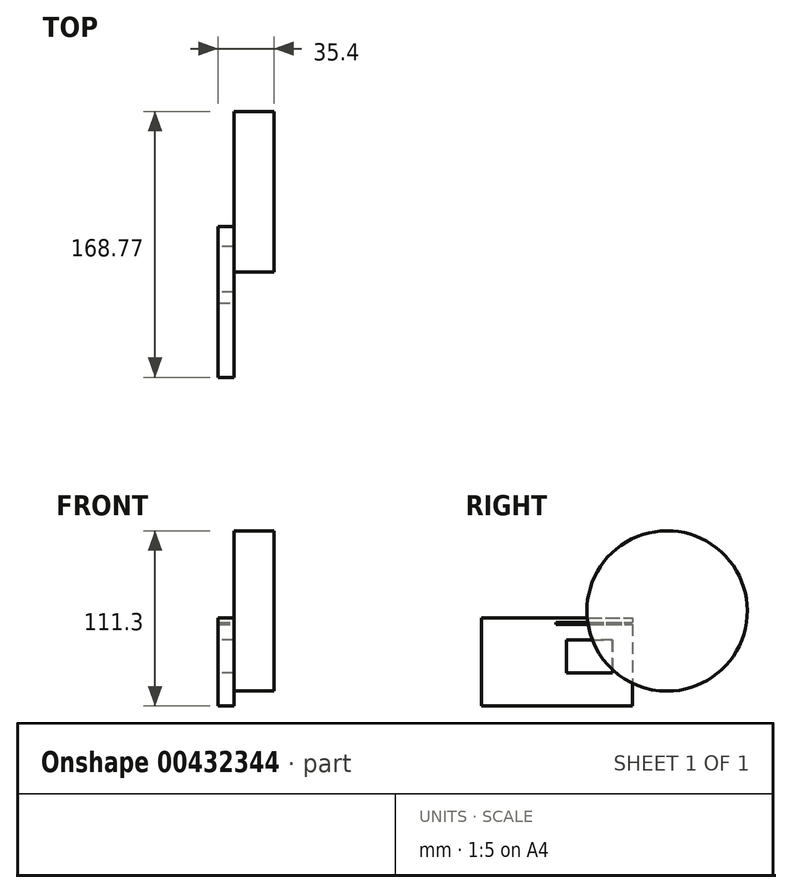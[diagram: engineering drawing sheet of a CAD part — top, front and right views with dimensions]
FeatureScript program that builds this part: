
annotation { "Feature Type Name" : "Feature", "Feature Type Description" : "" }
export const myFeature = defineFeature(function(context is Context, id is Id, definition is map)
    precondition{}
    {
        {
            var Q0;
            Q0=qCreatedBy(makeId("Right.planeOp"),FACE);
            var sketch = newSketch(context, id + "F0", { "sketchPlane" : qUnion([Q0])});
            skLineSegment(sketch, "E0.bottom", {"start": v(-16.06, 32.04) * mm, "end": v(33.06, 32.04) * mm});
            skLineSegment(sketch, "E0.top", {"start": v(-16.06, 31.05) * mm, "end": v(33.06, 31.05) * mm});
            skLineSegment(sketch, "E0.left", {"start": v(-16.06, 32.04) * mm, "end": v(-16.06, 31.05) * mm});
            skLineSegment(sketch, "E0.right", {"start": v(33.06, 32.04) * mm, "end": v(33.06, 31.05) * mm});
            skLineSegment(sketch, "E1.bottom", {"start": v(48.43, -48.08) * mm, "end": v(-31.43, -48.08) * mm});
            skLineSegment(sketch, "E1.top", {"start": v(48.43, -43.57) * mm, "end": v(-31.43, -43.57) * mm});
            skLineSegment(sketch, "E1.left", {"start": v(48.43, -48.08) * mm, "end": v(48.43, -43.57) * mm});
            skLineSegment(sketch, "E1.right", {"start": v(-31.43, -48.08) * mm, "end": v(-31.43, -43.57) * mm});
            skLineSegment(sketch, "E2.bottom", {"start": v(-63.27, 35.08) * mm, "end": v(32.62, 35.08) * mm});
            skLineSegment(sketch, "E2.top", {"start": v(-63.27, -20.9) * mm, "end": v(32.62, -20.9) * mm});
            skLineSegment(sketch, "E2.left", {"start": v(-63.27, 35.08) * mm, "end": v(-63.27, -20.9) * mm});
            skLineSegment(sketch, "E2.right", {"start": v(32.62, 35.08) * mm, "end": v(32.62, -20.9) * mm});
            skSolve(sketch);
        }
        {
            var Q0;
            {var subQ0=sQuery(id+"F0.wireOp",EDGE,"E0.left");Q0=makeQuery(id+"F0.imprint","IMPRINT",FACE,{"disambiguationData":[TD([[makeQuery(id+"F0.imprint","IMPRINT",EDGE,{"derivedFrom":subQ0}),-1.0]])]});}
            var sketch = newSketch(context, id + "F1", { "sketchPlane" : qUnion([Q0])});
            skSolve(sketch);
        }
        {
            var Q0;
            {var subQ0=sQuery(id+"F0.wireOp",EDGE,"E0.left");Q0=makeQuery(id+"F0.imprint","IMPRINT",FACE,{"disambiguationData":[TD([[makeQuery(id+"F0.imprint","IMPRINT",EDGE,{"derivedFrom":subQ0}),-1.0]])]});}
            extrude(context, id + "F2", {"entities" : qUnion([Q0]), "oppositeDirection" : true, "depth" : 10 * mm});
        }
        {
            var Q0;
            Q0=makeQuery(id+"F2.opExtrude","CAP_FACE",FACE,{"disambiguationData":[OSD([sQuery(id+"F0.wireOp",EDGE,"E0.bottom"),sQuery(id+"F0.wireOp",EDGE,"E0.top"),sQuery(id+"F0.wireOp",EDGE,"E0.left"),sQuery(id+"F0.wireOp",EDGE,"E2.bottom"),sQuery(id+"F0.wireOp",EDGE,"E2.top"),sQuery(id+"F0.wireOp",EDGE,"E2.left"),sQuery(id+"F0.wireOp",EDGE,"E2.right")])],"isStart":false});
            var sketch = newSketch(context, id + "F3", { "sketchPlane" : qUnion([Q0])});
            skLineSegment(sketch, "E3.bottom", {"start": v(-19.93, 20.97) * mm, "end": v(9.22, 20.97) * mm});
            skLineSegment(sketch, "E3.top", {"start": v(-19.93, 0) * mm, "end": v(9.22, 0) * mm});
            skLineSegment(sketch, "E3.left", {"start": v(-19.93, 20.97) * mm, "end": v(-19.93, 0) * mm});
            skLineSegment(sketch, "E3.right", {"start": v(9.22, 20.97) * mm, "end": v(9.22, 0) * mm});
            skSolve(sketch);
        }
        {
            var Q0;
            Q0=makeQuery(id+"F3.imprint","IMPRINT",FACE,{"disambiguationData":[TD([[makeQuery(id+"F3.imprint","IMPRINT",EDGE,{"derivedFrom":sQuery(id+"F3.wireOp",EDGE,"E3.bottom")}),-1.0]])]});
            extrude(context, id + "F4", {"entities" : qUnion([Q0]), "operationType" : NewBodyOperationType.REMOVE, "oppositeDirection" : true, "depth" : 25.4 * mm});
        }
        {
            var Q0;
            Q0=qCreatedBy(makeId("Right.planeOp"),FACE);
            var sketch = newSketch(context, id + "F5", { "sketchPlane" : qUnion([Q0])});
            skCircle(sketch, "E4", {"center": v(54.57, 39.47) * mm, "radius": 50.93 * mm});
            skSolve(sketch);
        }
        {
            var Q0;
            Q0=makeQuery(id+"F5.imprint","IMPRINT",FACE,{"disambiguationData":[TD([[makeQuery(id+"F5.imprint","IMPRINT",EDGE,{"derivedFrom":sQuery(id+"F5.wireOp",EDGE,"E4")}),1.0]])]});
            extrude(context, id + "F6", {"entities" : qUnion([Q0]), "operationType" : NewBodyOperationType.ADD, "depth" : 25.4 * mm});
        }
        {
            var Q0;
            Q0=makeQuery(id+"F6.opExtrude","CAP_FACE",FACE,{"disambiguationData":[OSD([sQuery(id+"F5.wireOp",EDGE,"E4")])],"isStart":false});
            extrude(context, id + "F7", {"entities" : qUnion([Q0]), "operationType" : NewBodyOperationType.ADD, "oppositeDirection" : true, "depth" : 25 * mm, "offsetDistance" : 25 * mm});
        }
    });
